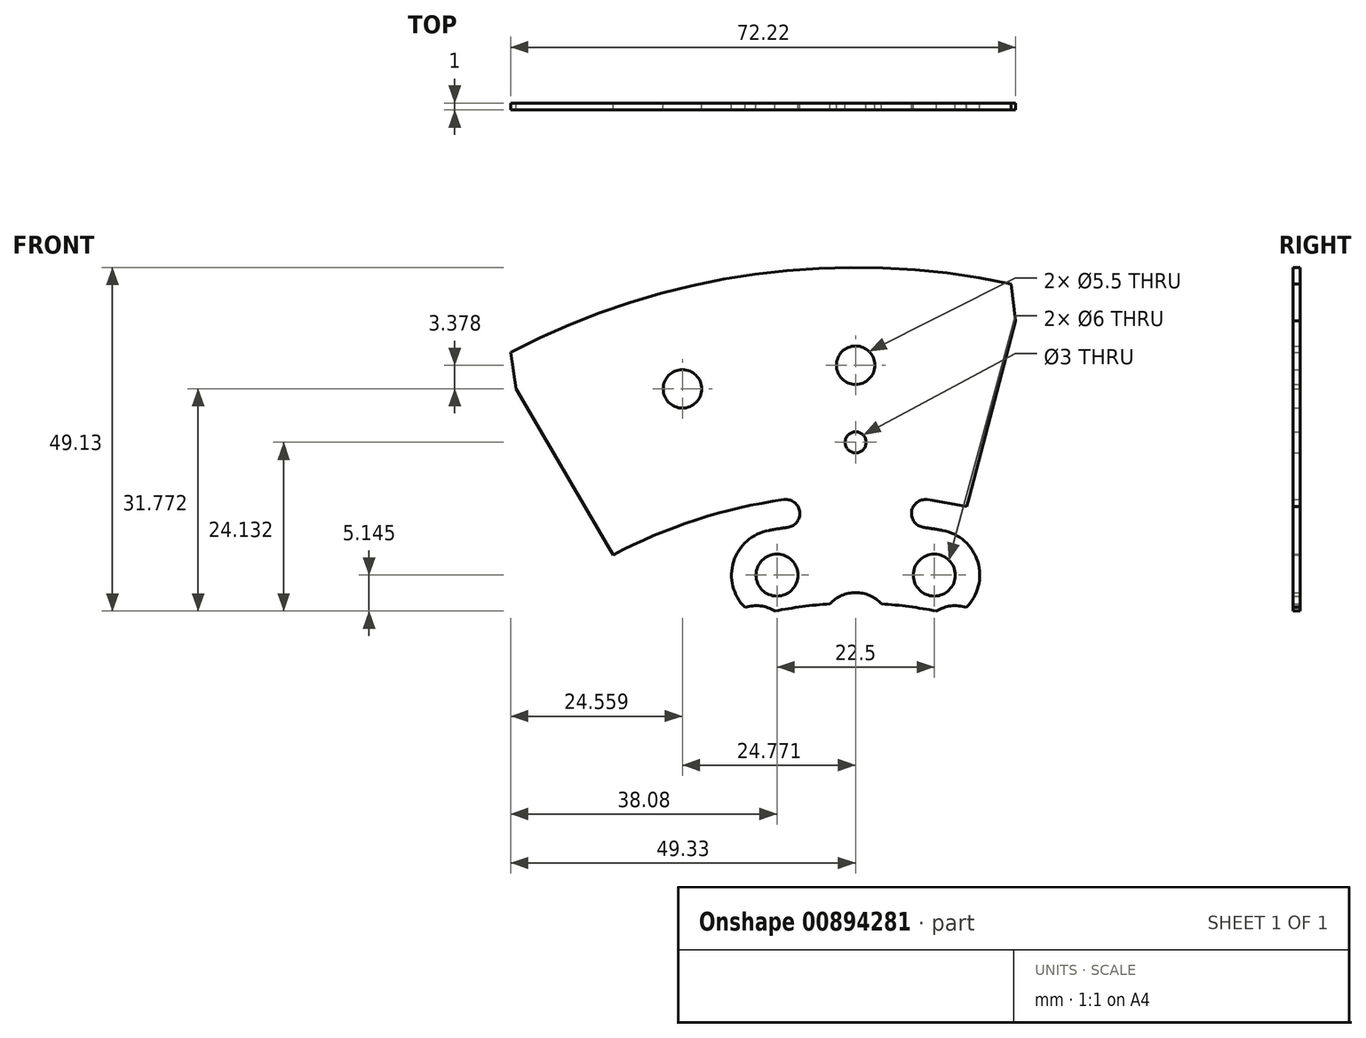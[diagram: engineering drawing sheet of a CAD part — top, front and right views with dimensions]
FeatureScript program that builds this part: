
annotation { "Feature Type Name" : "Feature", "Feature Type Description" : "" }
export const myFeature = defineFeature(function(context is Context, id is Id, definition is map)
    precondition{}
    {
        {
            var Q0;
            Q0=qCreatedBy(makeId("Front.planeOp"),FACE);
            var sketch = newSketch(context, id + "F0", { "sketchPlane" : qUnion([Q0])});
            skArc(sketch, "E0", {"start": v(44.56, 59.08) * mm, "mid": v(33.64, 65.9) * mm, "end": v(21.7, 70.75) * mm});
            skArc(sketch, "E1", {"start": v(15.9, 72.27) * mm, "mid": v(13.1, 72.83) * mm, "end": v(10.26, 73.29) * mm});
            skArc(sketch, "E2", {"start": v(42.16, 55.88) * mm, "mid": v(41.06, 56.7) * mm, "end": v(39.95, 57.48) * mm});
            skArc(sketch, "E3", {"start": v(12.4, 68.9) * mm, "mid": v(11.06, 69.12) * mm, "end": v(9.7, 69.32) * mm});
            skArc(sketch, "E4", {"start": v(10.26, 73.29) * mm, "mid": v(8, 71.58) * mm, "end": v(9.7, 69.32) * mm});
            skArc(sketch, "E5", {"start": v(42.16, 55.88) * mm, "mid": v(44.96, 56.27) * mm, "end": v(44.56, 59.08) * mm});
            skArc(sketch, "E6", {"start": v(-10.26, 73.29) * mm, "mid": v(-22.82, 70.4) * mm, "end": v(-34.68, 65.37) * mm});
            skArc(sketch, "E7", {"start": v(-39.86, 62.35) * mm, "mid": v(-42.24, 60.76) * mm, "end": v(-44.56, 59.08) * mm});
            skArc(sketch, "E8", {"start": v(-9.7, 69.32) * mm, "mid": v(-11.06, 69.12) * mm, "end": v(-12.4, 68.9) * mm});
            skArc(sketch, "E9", {"start": v(-39.95, 57.48) * mm, "mid": v(-41.06, 56.7) * mm, "end": v(-42.16, 55.88) * mm});
            skArc(sketch, "E10", {"start": v(-44.56, 59.08) * mm, "mid": v(-44.96, 56.27) * mm, "end": v(-42.16, 55.88) * mm});
            skArc(sketch, "E11", {"start": v(-9.7, 69.32) * mm, "mid": v(-8, 71.58) * mm, "end": v(-10.26, 73.29) * mm});
            skArc(sketch, "E12", {"start": v(-59.08, 44.56) * mm, "mid": v(-65.9, 33.64) * mm, "end": v(-70.75, 21.7) * mm});
            skArc(sketch, "E13", {"start": v(-72.27, 15.9) * mm, "mid": v(-72.83, 13.1) * mm, "end": v(-73.29, 10.26) * mm});
            skArc(sketch, "E14", {"start": v(-55.88, 42.16) * mm, "mid": v(-56.7, 41.06) * mm, "end": v(-57.48, 39.95) * mm});
            skArc(sketch, "E15", {"start": v(-68.9, 12.4) * mm, "mid": v(-69.12, 11.06) * mm, "end": v(-69.32, 9.7) * mm});
            skArc(sketch, "E16", {"start": v(-73.29, 10.26) * mm, "mid": v(-71.58, 8) * mm, "end": v(-69.32, 9.7) * mm});
            skArc(sketch, "E17", {"start": v(-55.88, 42.16) * mm, "mid": v(-56.27, 44.96) * mm, "end": v(-59.08, 44.56) * mm});
            skArc(sketch, "E18", {"start": v(-73.29, -10.26) * mm, "mid": v(-70.4, -22.82) * mm, "end": v(-65.37, -34.68) * mm});
            skArc(sketch, "E19", {"start": v(-62.35, -39.86) * mm, "mid": v(-60.76, -42.24) * mm, "end": v(-59.08, -44.56) * mm});
            skArc(sketch, "E20", {"start": v(-69.32, -9.7) * mm, "mid": v(-69.12, -11.06) * mm, "end": v(-68.9, -12.4) * mm});
            skArc(sketch, "E21", {"start": v(-57.48, -39.95) * mm, "mid": v(-56.7, -41.06) * mm, "end": v(-55.88, -42.16) * mm});
            skArc(sketch, "E22", {"start": v(-59.08, -44.56) * mm, "mid": v(-56.27, -44.96) * mm, "end": v(-55.88, -42.16) * mm});
            skArc(sketch, "E23", {"start": v(-69.32, -9.7) * mm, "mid": v(-71.58, -8) * mm, "end": v(-73.29, -10.26) * mm});
            skArc(sketch, "E24", {"start": v(-44.56, -59.08) * mm, "mid": v(-33.64, -65.9) * mm, "end": v(-21.7, -70.75) * mm});
            skArc(sketch, "E25", {"start": v(-15.9, -72.27) * mm, "mid": v(-13.1, -72.83) * mm, "end": v(-10.26, -73.29) * mm});
            skArc(sketch, "E26", {"start": v(-42.16, -55.88) * mm, "mid": v(-41.06, -56.7) * mm, "end": v(-39.95, -57.48) * mm});
            skArc(sketch, "E27", {"start": v(-12.4, -68.9) * mm, "mid": v(-11.06, -69.12) * mm, "end": v(-9.7, -69.32) * mm});
            skArc(sketch, "E28", {"start": v(-10.26, -73.29) * mm, "mid": v(-8, -71.58) * mm, "end": v(-9.7, -69.32) * mm});
            skArc(sketch, "E29", {"start": v(-42.16, -55.88) * mm, "mid": v(-44.96, -56.27) * mm, "end": v(-44.56, -59.08) * mm});
            skArc(sketch, "E30", {"start": v(10.26, -73.29) * mm, "mid": v(22.82, -70.4) * mm, "end": v(34.68, -65.37) * mm});
            skArc(sketch, "E31", {"start": v(39.86, -62.35) * mm, "mid": v(42.24, -60.76) * mm, "end": v(44.56, -59.08) * mm});
            skArc(sketch, "E32", {"start": v(9.7, -69.32) * mm, "mid": v(11.06, -69.12) * mm, "end": v(12.4, -68.9) * mm});
            skArc(sketch, "E33", {"start": v(39.95, -57.48) * mm, "mid": v(41.06, -56.7) * mm, "end": v(42.16, -55.88) * mm});
            skArc(sketch, "E34", {"start": v(44.56, -59.08) * mm, "mid": v(44.96, -56.27) * mm, "end": v(42.16, -55.88) * mm});
            skArc(sketch, "E35", {"start": v(9.7, -69.32) * mm, "mid": v(8, -71.58) * mm, "end": v(10.26, -73.29) * mm});
            skArc(sketch, "E36", {"start": v(59.08, -44.56) * mm, "mid": v(65.9, -33.64) * mm, "end": v(70.75, -21.7) * mm});
            skArc(sketch, "E37", {"start": v(72.27, -15.9) * mm, "mid": v(72.83, -13.1) * mm, "end": v(73.29, -10.26) * mm});
            skArc(sketch, "E38", {"start": v(55.88, -42.16) * mm, "mid": v(56.7, -41.06) * mm, "end": v(57.48, -39.95) * mm});
            skArc(sketch, "E39", {"start": v(68.9, -12.4) * mm, "mid": v(69.12, -11.06) * mm, "end": v(69.32, -9.7) * mm});
            skArc(sketch, "E40", {"start": v(73.29, -10.26) * mm, "mid": v(71.58, -8) * mm, "end": v(69.32, -9.7) * mm});
            skArc(sketch, "E41", {"start": v(55.88, -42.16) * mm, "mid": v(56.27, -44.96) * mm, "end": v(59.08, -44.56) * mm});
            skArc(sketch, "E42", {"start": v(73.29, 10.26) * mm, "mid": v(70.4, 22.82) * mm, "end": v(65.37, 34.68) * mm});
            skArc(sketch, "E43", {"start": v(62.35, 39.86) * mm, "mid": v(60.76, 42.24) * mm, "end": v(59.08, 44.56) * mm});
            skArc(sketch, "E44", {"start": v(69.32, 9.7) * mm, "mid": v(69.12, 11.06) * mm, "end": v(68.9, 12.4) * mm});
            skArc(sketch, "E45", {"start": v(57.48, 39.95) * mm, "mid": v(56.7, 41.06) * mm, "end": v(55.88, 42.16) * mm});
            skArc(sketch, "E46", {"start": v(59.08, 44.56) * mm, "mid": v(56.27, 44.96) * mm, "end": v(55.88, 42.16) * mm});
            skArc(sketch, "E47", {"start": v(69.32, 9.7) * mm, "mid": v(71.58, 8) * mm, "end": v(73.29, 10.26) * mm});
            skArc(sketch, "E48", {"start": v(11.56, 57.35) * mm, "mid": v(7.64, 58) * mm, "end": v(3.68, 58.38) * mm});
            skArc(sketch, "E49", {"start": v(-3.68, 58.38) * mm, "mid": v(-7.64, 58) * mm, "end": v(-11.56, 57.35) * mm});
            skArc(sketch, "E50", {"start": v(15.82, 57.87) * mm, "mid": v(17.72, 63.1) * mm, "end": v(14.88, 67.89) * mm});
            skArc(sketch, "E51", {"start": v(14.88, 67.89) * mm, "mid": v(13.7, 68.52) * mm, "end": v(12.4, 68.9) * mm});
            skArc(sketch, "E52", {"start": v(-12.4, 68.9) * mm, "mid": v(-13.7, 68.52) * mm, "end": v(-14.88, 67.89) * mm});
            skArc(sketch, "E53", {"start": v(-14.88, 67.89) * mm, "mid": v(-17.72, 63.1) * mm, "end": v(-15.82, 57.87) * mm});
            skArc(sketch, "E54", {"start": v(-32.38, 48.72) * mm, "mid": v(-35.61, 46.41) * mm, "end": v(-38.68, 43.89) * mm});
            skArc(sketch, "E55", {"start": v(-43.89, 38.68) * mm, "mid": v(-46.41, 35.61) * mm, "end": v(-48.72, 32.38) * mm});
            skArc(sketch, "E56", {"start": v(-29.74, 52.1) * mm, "mid": v(-32.09, 57.15) * mm, "end": v(-37.48, 58.52) * mm});
            skArc(sketch, "E57", {"start": v(-37.48, 58.52) * mm, "mid": v(-38.77, 58.13) * mm, "end": v(-39.95, 57.48) * mm});
            skArc(sketch, "E58", {"start": v(-57.48, 39.95) * mm, "mid": v(-58.13, 38.77) * mm, "end": v(-58.52, 37.48) * mm});
            skArc(sketch, "E59", {"start": v(-58.52, 37.48) * mm, "mid": v(-57.15, 32.09) * mm, "end": v(-52.1, 29.74) * mm});
            skArc(sketch, "E60", {"start": v(-57.35, 11.56) * mm, "mid": v(-58, 7.64) * mm, "end": v(-58.38, 3.68) * mm});
            skArc(sketch, "E61", {"start": v(-58.38, -3.68) * mm, "mid": v(-58, -7.64) * mm, "end": v(-57.35, -11.56) * mm});
            skArc(sketch, "E62", {"start": v(-57.87, 15.82) * mm, "mid": v(-63.1, 17.72) * mm, "end": v(-67.89, 14.88) * mm});
            skArc(sketch, "E63", {"start": v(-67.89, 14.88) * mm, "mid": v(-68.52, 13.7) * mm, "end": v(-68.9, 12.4) * mm});
            skArc(sketch, "E64", {"start": v(-68.9, -12.4) * mm, "mid": v(-68.52, -13.7) * mm, "end": v(-67.89, -14.88) * mm});
            skArc(sketch, "E65", {"start": v(-67.89, -14.88) * mm, "mid": v(-63.1, -17.72) * mm, "end": v(-57.87, -15.82) * mm});
            skArc(sketch, "E66", {"start": v(-48.72, -32.38) * mm, "mid": v(-46.41, -35.61) * mm, "end": v(-43.89, -38.68) * mm});
            skArc(sketch, "E67", {"start": v(-38.68, -43.89) * mm, "mid": v(-35.61, -46.41) * mm, "end": v(-32.38, -48.72) * mm});
            skArc(sketch, "E68", {"start": v(-52.1, -29.74) * mm, "mid": v(-57.15, -32.09) * mm, "end": v(-58.52, -37.48) * mm});
            skArc(sketch, "E69", {"start": v(-58.52, -37.48) * mm, "mid": v(-58.13, -38.77) * mm, "end": v(-57.48, -39.95) * mm});
            skArc(sketch, "E70", {"start": v(-39.95, -57.48) * mm, "mid": v(-38.77, -58.13) * mm, "end": v(-37.48, -58.52) * mm});
            skArc(sketch, "E71", {"start": v(-37.48, -58.52) * mm, "mid": v(-32.09, -57.15) * mm, "end": v(-29.74, -52.1) * mm});
            skArc(sketch, "E72", {"start": v(-11.56, -57.35) * mm, "mid": v(-7.64, -58) * mm, "end": v(-3.68, -58.38) * mm});
            skArc(sketch, "E73", {"start": v(3.68, -58.38) * mm, "mid": v(7.64, -58) * mm, "end": v(11.56, -57.35) * mm});
            skArc(sketch, "E74", {"start": v(-15.82, -57.87) * mm, "mid": v(-17.72, -63.1) * mm, "end": v(-14.88, -67.89) * mm});
            skArc(sketch, "E75", {"start": v(-14.88, -67.89) * mm, "mid": v(-13.7, -68.52) * mm, "end": v(-12.4, -68.9) * mm});
            skArc(sketch, "E76", {"start": v(12.4, -68.9) * mm, "mid": v(13.7, -68.52) * mm, "end": v(14.88, -67.89) * mm});
            skArc(sketch, "E77", {"start": v(14.88, -67.89) * mm, "mid": v(17.72, -63.1) * mm, "end": v(15.82, -57.87) * mm});
            skArc(sketch, "E78", {"start": v(32.38, -48.72) * mm, "mid": v(35.61, -46.41) * mm, "end": v(38.68, -43.89) * mm});
            skArc(sketch, "E79", {"start": v(43.89, -38.68) * mm, "mid": v(46.41, -35.61) * mm, "end": v(48.72, -32.38) * mm});
            skArc(sketch, "E80", {"start": v(29.74, -52.1) * mm, "mid": v(32.09, -57.15) * mm, "end": v(37.48, -58.52) * mm});
            skArc(sketch, "E81", {"start": v(37.48, -58.52) * mm, "mid": v(38.77, -58.13) * mm, "end": v(39.95, -57.48) * mm});
            skArc(sketch, "E82", {"start": v(57.48, -39.95) * mm, "mid": v(58.13, -38.77) * mm, "end": v(58.52, -37.48) * mm});
            skArc(sketch, "E83", {"start": v(58.52, -37.48) * mm, "mid": v(57.15, -32.09) * mm, "end": v(52.1, -29.74) * mm});
            skArc(sketch, "E84", {"start": v(57.35, -11.56) * mm, "mid": v(58, -7.64) * mm, "end": v(58.38, -3.68) * mm});
            skArc(sketch, "E85", {"start": v(58.38, 3.68) * mm, "mid": v(58, 7.64) * mm, "end": v(57.35, 11.56) * mm});
            skArc(sketch, "E86", {"start": v(57.87, -15.82) * mm, "mid": v(63.1, -17.72) * mm, "end": v(67.89, -14.88) * mm});
            skArc(sketch, "E87", {"start": v(67.89, -14.88) * mm, "mid": v(68.52, -13.7) * mm, "end": v(68.9, -12.4) * mm});
            skArc(sketch, "E88", {"start": v(68.9, 12.4) * mm, "mid": v(68.52, 13.7) * mm, "end": v(67.89, 14.88) * mm});
            skArc(sketch, "E89", {"start": v(67.89, 14.88) * mm, "mid": v(63.1, 17.72) * mm, "end": v(57.87, 15.82) * mm});
            skArc(sketch, "E90", {"start": v(48.72, 32.38) * mm, "mid": v(46.41, 35.61) * mm, "end": v(43.89, 38.68) * mm});
            skArc(sketch, "E91", {"start": v(38.68, 43.89) * mm, "mid": v(35.61, 46.41) * mm, "end": v(32.38, 48.72) * mm});
            skArc(sketch, "E92", {"start": v(52.1, 29.74) * mm, "mid": v(57.15, 32.09) * mm, "end": v(58.52, 37.48) * mm});
            skArc(sketch, "E93", {"start": v(58.52, 37.48) * mm, "mid": v(58.13, 38.77) * mm, "end": v(57.48, 39.95) * mm});
            skArc(sketch, "E94", {"start": v(39.95, 57.48) * mm, "mid": v(38.77, 58.13) * mm, "end": v(37.48, 58.52) * mm});
            skArc(sketch, "E95", {"start": v(37.48, 58.52) * mm, "mid": v(32.09, 57.15) * mm, "end": v(29.74, 52.1) * mm});
            skArc(sketch, "E96", {"start": v(3.68, 58.38) * mm, "mid": v(0, 60) * mm, "end": v(-3.68, 58.38) * mm});
            skArc(sketch, "E97", {"start": v(-38.68, 43.89) * mm, "mid": v(-42.43, 42.43) * mm, "end": v(-43.89, 38.68) * mm});
            skArc(sketch, "E98", {"start": v(-58.38, 3.68) * mm, "mid": v(-60, 0) * mm, "end": v(-58.38, -3.68) * mm});
            skArc(sketch, "E99", {"start": v(-43.89, -38.68) * mm, "mid": v(-42.43, -42.43) * mm, "end": v(-38.68, -43.89) * mm});
            skArc(sketch, "E100", {"start": v(-3.68, -58.38) * mm, "mid": v(0, -60) * mm, "end": v(3.68, -58.38) * mm});
            skArc(sketch, "E101", {"start": v(38.68, -43.89) * mm, "mid": v(42.43, -42.43) * mm, "end": v(43.89, -38.68) * mm});
            skArc(sketch, "E102", {"start": v(58.38, -3.68) * mm, "mid": v(60, 0) * mm, "end": v(58.38, 3.68) * mm});
            skArc(sketch, "E103", {"start": v(43.89, 38.68) * mm, "mid": v(42.43, 42.43) * mm, "end": v(38.68, 43.89) * mm});
            skArc(sketch, "E104", {"start": v(-52.1, -29.74) * mm, "mid": v(-50.71, -31.44) * mm, "end": v(-48.72, -32.38) * mm});
            skArc(sketch, "E105", {"start": v(-15.82, -57.87) * mm, "mid": v(-13.63, -58.09) * mm, "end": v(-11.56, -57.35) * mm});
            skArc(sketch, "E106", {"start": v(29.74, -52.1) * mm, "mid": v(31.44, -50.71) * mm, "end": v(32.38, -48.72) * mm});
            skArc(sketch, "E107", {"start": v(57.87, -15.82) * mm, "mid": v(58.09, -13.63) * mm, "end": v(57.35, -11.56) * mm});
            skArc(sketch, "E108", {"start": v(52.1, 29.74) * mm, "mid": v(50.71, 31.44) * mm, "end": v(48.72, 32.38) * mm});
            skArc(sketch, "E109", {"start": v(15.82, 57.87) * mm, "mid": v(13.63, 58.09) * mm, "end": v(11.56, 57.35) * mm});
            skArc(sketch, "E110", {"start": v(-29.74, 52.1) * mm, "mid": v(-31.44, 50.71) * mm, "end": v(-32.38, 48.72) * mm});
            skArc(sketch, "E111", {"start": v(-57.87, 15.82) * mm, "mid": v(-58.09, 13.63) * mm, "end": v(-57.35, 11.56) * mm});
            skArc(sketch, "E112", {"start": v(48.72, -32.38) * mm, "mid": v(50.71, -31.44) * mm, "end": v(52.1, -29.74) * mm});
            skArc(sketch, "E113", {"start": v(57.35, 11.56) * mm, "mid": v(58.09, 13.63) * mm, "end": v(57.87, 15.82) * mm});
            skArc(sketch, "E114", {"start": v(32.38, 48.72) * mm, "mid": v(31.44, 50.71) * mm, "end": v(29.74, 52.1) * mm});
            skArc(sketch, "E115", {"start": v(-11.56, 57.35) * mm, "mid": v(-13.63, 58.09) * mm, "end": v(-15.82, 57.87) * mm});
            skArc(sketch, "E116", {"start": v(-48.72, 32.38) * mm, "mid": v(-50.71, 31.44) * mm, "end": v(-52.1, 29.74) * mm});
            skArc(sketch, "E117", {"start": v(-57.35, -11.56) * mm, "mid": v(-58.09, -13.63) * mm, "end": v(-57.87, -15.82) * mm});
            skArc(sketch, "E118", {"start": v(-32.38, -48.72) * mm, "mid": v(-31.44, -50.71) * mm, "end": v(-29.74, -52.1) * mm});
            skArc(sketch, "E119", {"start": v(11.56, -57.35) * mm, "mid": v(13.63, -58.09) * mm, "end": v(15.82, -57.87) * mm});
            skLineSegment(sketch, "E120", {"start": v(15.9, 72.27) * mm, "end": v(16.29, 73.72) * mm});
            skLineSegment(sketch, "E121", {"start": v(16.29, 73.72) * mm, "end": v(22.89, 98.87) * mm});
            skLineSegment(sketch, "E122", {"start": v(21.7, 70.75) * mm, "end": v(22.08, 72.2) * mm});
            skLineSegment(sketch, "E123", {"start": v(22.08, 72.2) * mm, "end": v(28.69, 97.34) * mm});
            skLineSegment(sketch, "E124", {"start": v(22.23, 104.13) * mm, "end": v(22.89, 98.87) * mm});
            skLineSegment(sketch, "E125", {"start": v(28.69, 97.34) * mm, "end": v(31.84, 101.6) * mm});
            skLineSegment(sketch, "E126", {"start": v(-39.86, 62.35) * mm, "end": v(-40.61, 63.65) * mm});
            skLineSegment(sketch, "E127", {"start": v(-40.61, 63.65) * mm, "end": v(-53.72, 86.1) * mm});
            skLineSegment(sketch, "E128", {"start": v(-34.68, 65.37) * mm, "end": v(-35.44, 66.67) * mm});
            skLineSegment(sketch, "E129", {"start": v(-35.44, 66.67) * mm, "end": v(-48.55, 89.12) * mm});
            skLineSegment(sketch, "E130", {"start": v(-57.91, 89.36) * mm, "end": v(-53.72, 86.1) * mm});
            skLineSegment(sketch, "E131", {"start": v(-48.55, 89.12) * mm, "end": v(-49.33, 94.37) * mm});
            skLineSegment(sketch, "E132", {"start": v(-72.27, 15.9) * mm, "end": v(-73.72, 16.29) * mm});
            skLineSegment(sketch, "E133", {"start": v(-73.72, 16.29) * mm, "end": v(-98.87, 22.89) * mm});
            skLineSegment(sketch, "E134", {"start": v(-70.75, 21.7) * mm, "end": v(-72.2, 22.08) * mm});
            skLineSegment(sketch, "E135", {"start": v(-72.2, 22.08) * mm, "end": v(-97.34, 28.69) * mm});
            skLineSegment(sketch, "E136", {"start": v(-104.13, 22.23) * mm, "end": v(-98.87, 22.89) * mm});
            skLineSegment(sketch, "E137", {"start": v(-97.34, 28.69) * mm, "end": v(-101.6, 31.84) * mm});
            skLineSegment(sketch, "E138", {"start": v(-62.35, -39.86) * mm, "end": v(-63.65, -40.61) * mm});
            skLineSegment(sketch, "E139", {"start": v(-63.65, -40.61) * mm, "end": v(-86.1, -53.72) * mm});
            skLineSegment(sketch, "E140", {"start": v(-65.37, -34.68) * mm, "end": v(-66.67, -35.44) * mm});
            skLineSegment(sketch, "E141", {"start": v(-66.67, -35.44) * mm, "end": v(-89.12, -48.55) * mm});
            skLineSegment(sketch, "E142", {"start": v(-89.36, -57.91) * mm, "end": v(-86.1, -53.72) * mm});
            skLineSegment(sketch, "E143", {"start": v(-89.12, -48.55) * mm, "end": v(-94.37, -49.33) * mm});
            skLineSegment(sketch, "E144", {"start": v(-15.9, -72.27) * mm, "end": v(-16.29, -73.72) * mm});
            skLineSegment(sketch, "E145", {"start": v(-16.29, -73.72) * mm, "end": v(-22.89, -98.87) * mm});
            skLineSegment(sketch, "E146", {"start": v(-21.7, -70.75) * mm, "end": v(-22.08, -72.2) * mm});
            skLineSegment(sketch, "E147", {"start": v(-22.08, -72.2) * mm, "end": v(-28.69, -97.34) * mm});
            skLineSegment(sketch, "E148", {"start": v(-22.23, -104.13) * mm, "end": v(-22.89, -98.87) * mm});
            skLineSegment(sketch, "E149", {"start": v(-28.69, -97.34) * mm, "end": v(-31.84, -101.6) * mm});
            skLineSegment(sketch, "E150", {"start": v(39.86, -62.35) * mm, "end": v(40.61, -63.65) * mm});
            skLineSegment(sketch, "E151", {"start": v(40.61, -63.65) * mm, "end": v(53.72, -86.1) * mm});
            skLineSegment(sketch, "E152", {"start": v(34.68, -65.37) * mm, "end": v(35.44, -66.67) * mm});
            skLineSegment(sketch, "E153", {"start": v(35.44, -66.67) * mm, "end": v(48.55, -89.12) * mm});
            skLineSegment(sketch, "E154", {"start": v(57.91, -89.36) * mm, "end": v(53.72, -86.1) * mm});
            skLineSegment(sketch, "E155", {"start": v(48.55, -89.12) * mm, "end": v(49.33, -94.37) * mm});
            skLineSegment(sketch, "E156", {"start": v(72.27, -15.9) * mm, "end": v(73.72, -16.29) * mm});
            skLineSegment(sketch, "E157", {"start": v(73.72, -16.29) * mm, "end": v(98.87, -22.89) * mm});
            skLineSegment(sketch, "E158", {"start": v(70.75, -21.7) * mm, "end": v(72.2, -22.08) * mm});
            skLineSegment(sketch, "E159", {"start": v(72.2, -22.08) * mm, "end": v(97.34, -28.69) * mm});
            skLineSegment(sketch, "E160", {"start": v(104.13, -22.23) * mm, "end": v(98.87, -22.89) * mm});
            skLineSegment(sketch, "E161", {"start": v(97.34, -28.69) * mm, "end": v(101.6, -31.84) * mm});
            skLineSegment(sketch, "E162", {"start": v(62.35, 39.86) * mm, "end": v(63.65, 40.61) * mm});
            skLineSegment(sketch, "E163", {"start": v(63.65, 40.61) * mm, "end": v(86.1, 53.72) * mm});
            skLineSegment(sketch, "E164", {"start": v(65.37, 34.68) * mm, "end": v(66.67, 35.44) * mm});
            skLineSegment(sketch, "E165", {"start": v(66.67, 35.44) * mm, "end": v(89.12, 48.55) * mm});
            skLineSegment(sketch, "E166", {"start": v(89.36, 57.91) * mm, "end": v(86.1, 53.72) * mm});
            skLineSegment(sketch, "E167", {"start": v(89.12, 48.55) * mm, "end": v(94.37, 49.33) * mm});
            skArc(sketch, "E168", {"start": v(22.23, 104.13) * mm, "mid": v(-14.4, 105.5) * mm, "end": v(-49.33, 94.37) * mm});
            skArc(sketch, "E169", {"start": v(-57.91, 89.36) * mm, "mid": v(-84.79, 64.42) * mm, "end": v(-101.6, 31.84) * mm});
            skArc(sketch, "E170", {"start": v(-104.13, 22.23) * mm, "mid": v(-105.5, -14.4) * mm, "end": v(-94.37, -49.33) * mm});
            skArc(sketch, "E171", {"start": v(-89.36, -57.91) * mm, "mid": v(-64.42, -84.79) * mm, "end": v(-31.84, -101.6) * mm});
            skArc(sketch, "E172", {"start": v(-22.23, -104.13) * mm, "mid": v(14.4, -105.5) * mm, "end": v(49.33, -94.37) * mm});
            skArc(sketch, "E173", {"start": v(57.91, -89.36) * mm, "mid": v(84.79, -64.42) * mm, "end": v(101.6, -31.84) * mm});
            skArc(sketch, "E174", {"start": v(104.13, -22.23) * mm, "mid": v(105.5, 14.4) * mm, "end": v(94.37, 49.33) * mm});
            skArc(sketch, "E175", {"start": v(89.36, 57.91) * mm, "mid": v(64.42, 84.79) * mm, "end": v(31.84, 101.6) * mm});
            skCircle(sketch, "E176", {"center": v(0, 81.48) * mm, "radius": 1.5 * mm});
            skCircle(sketch, "E177", {"center": v(-57.62, 57.62) * mm, "radius": 1.5 * mm});
            skCircle(sketch, "E178", {"center": v(-81.48, 0) * mm, "radius": 1.5 * mm});
            skCircle(sketch, "E179", {"center": v(-57.62, -57.62) * mm, "radius": 1.5 * mm});
            skCircle(sketch, "E180", {"center": v(0, -81.48) * mm, "radius": 1.5 * mm});
            skCircle(sketch, "E181", {"center": v(57.62, -57.62) * mm, "radius": 1.5 * mm});
            skCircle(sketch, "E182", {"center": v(81.48, 0) * mm, "radius": 1.5 * mm});
            skCircle(sketch, "E183", {"center": v(57.62, 57.62) * mm, "radius": 1.5 * mm});
            skCircle(sketch, "E184", {"center": v(0, 92.5) * mm, "radius": 2.75 * mm});
            skCircle(sketch, "E185", {"center": v(-65.4, 65.4) * mm, "radius": 2.75 * mm});
            skCircle(sketch, "E186", {"center": v(-92.5, 0) * mm, "radius": 2.75 * mm});
            skCircle(sketch, "E187", {"center": v(-65.4, -65.4) * mm, "radius": 2.75 * mm});
            skCircle(sketch, "E188", {"center": v(0, -92.5) * mm, "radius": 2.75 * mm});
            skCircle(sketch, "E189", {"center": v(65.4, -65.4) * mm, "radius": 2.75 * mm});
            skCircle(sketch, "E190", {"center": v(92.5, 0) * mm, "radius": 2.75 * mm});
            skCircle(sketch, "E191", {"center": v(65.4, 65.4) * mm, "radius": 2.75 * mm});
            skCircle(sketch, "E192", {"center": v(-24.77, 89.12) * mm, "radius": 2.75 * mm});
            skCircle(sketch, "E193", {"center": v(-80.53, 45.5) * mm, "radius": 2.75 * mm});
            skCircle(sketch, "E194", {"center": v(-89.12, -24.77) * mm, "radius": 2.75 * mm});
            skCircle(sketch, "E195", {"center": v(-45.5, -80.53) * mm, "radius": 2.75 * mm});
            skCircle(sketch, "E196", {"center": v(24.77, -89.12) * mm, "radius": 2.75 * mm});
            skCircle(sketch, "E197", {"center": v(80.53, -45.5) * mm, "radius": 2.75 * mm});
            skCircle(sketch, "E198", {"center": v(89.12, 24.77) * mm, "radius": 2.75 * mm});
            skCircle(sketch, "E199", {"center": v(45.5, 80.53) * mm, "radius": 2.75 * mm});
            skCircle(sketch, "E200", {"center": v(11.25, 62.5) * mm, "radius": 3 * mm});
            skCircle(sketch, "E201", {"center": v(-11.25, 62.5) * mm, "radius": 3 * mm});
            skCircle(sketch, "E202", {"center": v(-36.24, 52.15) * mm, "radius": 3 * mm});
            skCircle(sketch, "E203", {"center": v(-52.15, 36.24) * mm, "radius": 3 * mm});
            skCircle(sketch, "E204", {"center": v(-62.5, 11.25) * mm, "radius": 3 * mm});
            skCircle(sketch, "E205", {"center": v(-62.5, -11.25) * mm, "radius": 3 * mm});
            skCircle(sketch, "E206", {"center": v(-52.15, -36.24) * mm, "radius": 3 * mm});
            skCircle(sketch, "E207", {"center": v(-36.24, -52.15) * mm, "radius": 3 * mm});
            skCircle(sketch, "E208", {"center": v(-11.25, -62.5) * mm, "radius": 3 * mm});
            skCircle(sketch, "E209", {"center": v(11.25, -62.5) * mm, "radius": 3 * mm});
            skCircle(sketch, "E210", {"center": v(36.24, -52.15) * mm, "radius": 3 * mm});
            skCircle(sketch, "E211", {"center": v(52.15, -36.24) * mm, "radius": 3 * mm});
            skCircle(sketch, "E212", {"center": v(62.5, -11.25) * mm, "radius": 3 * mm});
            skCircle(sketch, "E213", {"center": v(52.15, 36.24) * mm, "radius": 3 * mm});
            skCircle(sketch, "E214", {"center": v(36.24, 52.15) * mm, "radius": 3 * mm});
            skCircle(sketch, "E215", {"center": v(62.5, 11.25) * mm, "radius": 3 * mm});
            skSolve(sketch);
        }
        {
            var Q0;
            Q0=makeQuery(id+"F0.imprint","IMPRINT",FACE,{"disambiguationData":[TD([[makeQuery(id+"F0.imprint","IMPRINT",EDGE,{"derivedFrom":sQuery(id+"F0.wireOp",EDGE,"E1")}),-1.0]])]});
            extrude(context, id + "F1", {"entities" : qUnion([Q0]), "depth" : 1 * mm, "offsetDistance" : 25 * mm});
        }
    });
